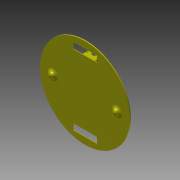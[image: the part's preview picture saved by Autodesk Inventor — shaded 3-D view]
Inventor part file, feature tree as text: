
AUTODESK INVENTOR PART (.ipt)
format: ipt  version: 2015 (Build 190159000, 159)  size: 424,448 bytes
history: native  units: mm
features: extrude x12, fillet x8, sketch x7, other x1, revolve x1
ambient origin geometry x8: Origin, YZ Plane, XZ Plane, XY Plane, X Axis, Y Axis, Z Axis, Center Point
bodies: Body1 (feature_tree)
feature tree (29):
  other  "Sólido1"
  sketch  "Boceto1"  dims[d0=37.0mm d1=57.0mm]
  extrude  "Extrusión1"  Depth=57.0mm
  extrude  "Extrusión2"  Depth=10.0mm
  extrude  "Extrusión3"  Depth=57.0mm
  sketch  "Boceto3"  dims[d4=20.0mm d5=57.0mm]
  extrude  "Extrusión4"  Depth=79.0mm
  extrude  "Extrusión5"  Depth=36.0mm
  extrude  "Extrusión6"  Depth=72.0mm
  extrude  "Extrusión7"  Depth=8.0mm
  fillet  "Empalme2"  Radius=3.0mm
  fillet  "Empalme3"  Radius=40.0mm
  fillet  "Empalme4"  Radius=13.0mm
  fillet  "Empalme5"  Radius=1111.0mm
  extrude  "Extrusión10"  Depth=8.0mm TaperAngle=0.0deg
  fillet  "Empalme10"  Radius=5.0mm
  sketch  "Boceto6"  dims[d6=37.0mm d7=79.0mm]
  extrude  "Extrusión11"  Depth=8.0mm TaperAngle=0.0deg
  extrude  "Extrusión12"  Depth=3.0mm TaperAngle=0.0deg
  fillet  "Empalme11"  Radius=1.0mm
  fillet  "Empalme12"  Radius=5.0mm
  revolve  "Revolución1"  [1 undecoded]
  fillet  "Empalme13"  Radius=2.0mm
  extrude  "Extrusión14"  Depth=3.0mm TaperAngle=0.0deg
  extrude  "Extrusión15"  Depth=1.0mm
  sketch  "Boceto2"  dims[d2=20.0mm d3=10.0mm]
  sketch  "Boceto8"  dims[d8=6.0mm d9=36.0mm]
  sketch  "Boceto9"  dims[d10=7.0mm d11=72.0mm]
  sketch  "Boceto10"  dims[d16=290.0mm d17=5.0mm d18=3.0mm d19=0.0mm d20=40.0mm d21=0.0mm d22=13.0mm d23=1111.0mm d24=0.0mm d25=5.0mm d26=0.0mm d27=5.0mm d28=0.0mm d29=111.0mm d30=0.0mm d31=3.0mm d32=0.0mm d41=1.0mm d42=5.0mm d43=5.0mm d44=2.0mm d47=3.0mm d48=0.0mm d51=1.0mm d53=2.5mm d54=6.5mm d55=3.0mm d56=0.0mm d57=3.0mm d58=0.0mm d59=1.0mm d60=2.0mm d63=19.5mm d64=19.5mm d65=180.0deg d66=10.0mm d67=270.0mm d68=10.0mm d69=0.0mm d70=292.0mm d71=300.0mm d72=270.0mm d73=10.0mm d74=6.0mm d75=3.0mm d76=0.5mm d77=35.0mm d78=3.0mm d79=0.5mm d80=6.0mm d81=35.0mm d82=40.0mm d84=360.0deg d86=8.0mm d87=0.0mm]
note: 1 required parameter value undecoded (feature->parameter linkage not recoverable at this tier; creation-order binding heuristic only, values carry confidence <= 0.55)
